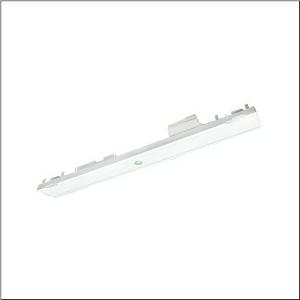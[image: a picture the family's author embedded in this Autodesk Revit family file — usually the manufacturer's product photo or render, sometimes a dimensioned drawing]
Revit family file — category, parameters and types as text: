
# Revit family: licross_r_56tl1e7c4x31_1f0a
name_source: partatom
category: Lighting Fixtures
units: mm (PartAtom-declared; Revit-internal decimal feet)

## family parameters
Cut with Voids When Loaded = No
Host = Face
Light Source = No
Part Type = Normal
Room Calculation Point = No
Round Connector Dimension = Use Diameter
Shared = No

## types (1)
- Licross® (1 x LED, 320 lm, 3.9 W, 4000K)
    Apparent Load = 4 VA
    CIE Flux Codes = 63 91 97 100 100
    Color Rendering = 70
    Color Temperature = 4000K
    Default Elevation = 1800 mm
    Description = Licross®, luminaire insert, of sheet steel, coil coated, white, length: 500mm, width: 59mm, height: 60mm, mounting height: 7..17m, emergency light element,LED rated luminous flux: 320lm, light colour: 740, control gear: CEAG, with plug, 6-pole, with phase selection, mains connection: 220..240V, AC/DC, 0/50..60Hz, rated input power: 3.9W, halogen-free wiring, for trunking rail, 9..14-core, for emergency light function, supply monitoring module CEAG, with address switch, choice between two emergency light lines via tool-free moving of contact pin prior to installation in trunking rail, primary light control with lens, of PMMA, primary optical cover: cover, of PMMA, light emission: direct distribution, primary light characteristic: asymmetric,  for escape and rescue routes, compatible with all CEAG STAR technology systems (ZB-S, DG-S (DualGuard-S), LP-STAR, AT-S+), protection rating (complete): IP40, insulation class (complete): insulation class I (protective earthing), certification: CE, UKCA, protection symbol: D if used in an environment without relevant dust loads, impact resistance: IK06, permissible ambient temperature for indoor applications: -20..+40°C, packaging unit: 1 piece
    Height = 60 mm  [stored 0.19685 ft]
    Lamp = 1 x LED
    Lamp Light Flux = 320 lm
    Lamp Power = 3.9 W
    Lamp count = 1
    Length = 500 mm  [stored 1.64042 ft]
    Luminous efficacy = 82 lm/W
    Manufacturer = Siteco
    ModVariant = No
    Model = 56TL1E7C4X31
    Mounting Place = Ceiling
    Mounting Type = Pendant
    Number of Poles = 1
    OnlyDefault = Yes
    Power Factor = 1
    Product Name = Licross®
    Product group = luminaire insert
    ProductGroupID = 902
    Protection Class = Protection class I
    Protection Degree = IP 40
    RLX_Detail_Level = 1
    RLX_Emergency_Light_Flux = 0 lm
    RLX_Emergency_Type = 0
    RLX_Emergency_Type_DB = No
    RlxData = <blob elided: 17957 chars, md5=37fd4382>
    Socket = socket
    Standby Power = 0 W
    System Light Flux = 320 lm
    System Power = 4 W
    Type Comments = Product without accessories
    Type Image = l_1251804.jpg
    URL = http://relux.com
    VarID = ---
    Voltage = 0 V
    Weight = 0.00 kg
    Width = 59 mm

note: [stored X ft] marks values corroborated as IEEE doubles in the binary element streams (Revit-internal decimal feet)

## geometry (parser evidence)
native form markers: Blend x4, Sweep x11
no freeform markers — native parametric forms only
